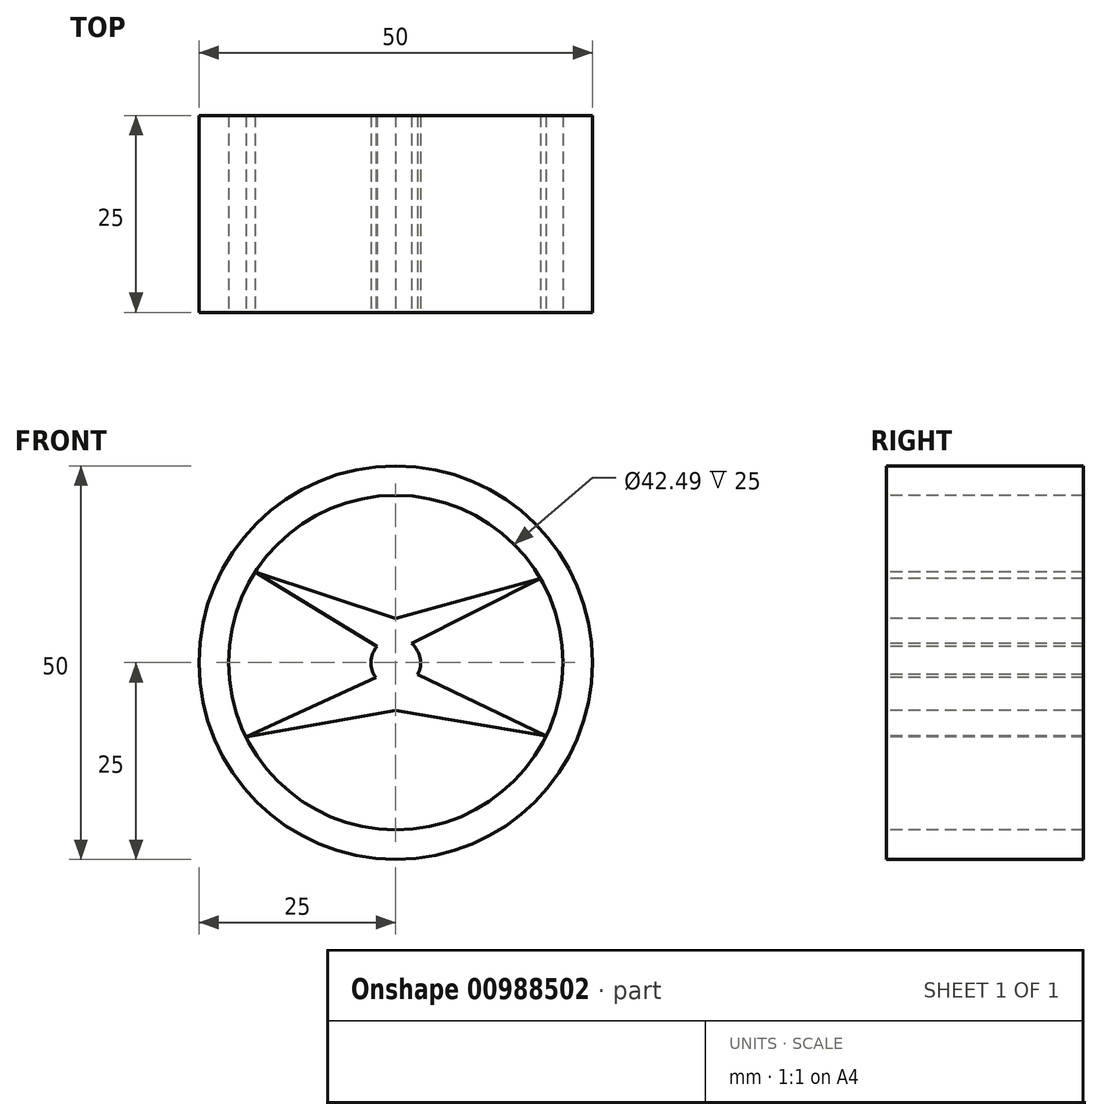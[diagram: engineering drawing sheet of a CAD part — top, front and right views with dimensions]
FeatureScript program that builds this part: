
annotation { "Feature Type Name" : "Feature", "Feature Type Description" : "" }
export const myFeature = defineFeature(function(context is Context, id is Id, definition is map)
    precondition{}
    {
        {
            var Q0;
            Q0=qCreatedBy(makeId("Front.planeOp"),FACE);
            var sketch = newSketch(context, id + "F0", { "sketchPlane" : qUnion([Q0])});
            skCircle(sketch, "E0", {"center": v(0, 0) * mm, "radius": 25 * mm});
            skSolve(sketch);
        }
        {
            var Q0;
            Q0=makeQuery(id+"F0.imprint","IMPRINT",FACE,{"disambiguationData":[TD([[makeQuery(id+"F0.imprint","IMPRINT",EDGE,{"derivedFrom":sQuery(id+"F0.wireOp",EDGE,"E0")}),1.0]])]});
            extrude(context, id + "F1", {"entities" : qUnion([Q0]), "depth" : 25 * mm, "offsetDistance" : 25 * mm});
        }
        {
            var Q0;
            Q0=makeQuery(id+"F1.opExtrude","CAP_FACE",FACE,{"disambiguationData":[OSD([sQuery(id+"F0.wireOp",EDGE,"E0")])],"isStart":false});
            var sketch = newSketch(context, id + "F2", { "sketchPlane" : qUnion([Q0])});
            skCircle(sketch, "E1", {"center": v(0, 0) * mm, "radius": 21.24 * mm});
            skCircle(sketch, "E2", {"center": v(0, 0) * mm, "radius": 3.16 * mm});
            skLineSegment(sketch, "E3", {"start": v(-2.52, -1.9) * mm, "end": v(-19.03, -9.44) * mm});
            skLineSegment(sketch, "E4", {"start": v(-19.03, -9.44) * mm, "end": v(0, -6.08) * mm});
            skLineSegment(sketch, "E5", {"start": v(0, -6.08) * mm, "end": v(19.08, -9.34) * mm});
            skLineSegment(sketch, "E6", {"start": v(19.08, -9.34) * mm, "end": v(2.77, -1.5) * mm});
            skLineSegment(sketch, "E7", {"start": v(2.04, 2.4) * mm, "end": v(18.36, 10.69) * mm});
            skLineSegment(sketch, "E8", {"start": v(18.36, 10.69) * mm, "end": v(0, 5.62) * mm});
            skLineSegment(sketch, "E9", {"start": v(0, 5.62) * mm, "end": v(-17.86, 11.5) * mm});
            skLineSegment(sketch, "E10", {"start": v(-17.86, 11.5) * mm, "end": v(-2.4, 2.06) * mm});
            skSolve(sketch);
        }
        {
            var Q0;
            {var subQ0=sQuery(id+"F2.wireOp",EDGE,"E8");Q0=makeQuery(id+"F2.imprint","IMPRINT",FACE,{"disambiguationData":[TD([[makeQuery(id+"F2.imprint","IMPRINT",EDGE,{"derivedFrom":subQ0}),-1.0]])]});}
            var Q1;
            {var subQ0=sQuery(id+"F2.wireOp",EDGE,"E4");Q1=makeQuery(id+"F2.imprint","IMPRINT",FACE,{"disambiguationData":[TD([[makeQuery(id+"F2.imprint","IMPRINT",EDGE,{"derivedFrom":subQ0}),-1.0]])]});}
            extrude(context, id + "F3", {"entities" : qUnion([Q0, Q1]), "operationType" : NewBodyOperationType.REMOVE, "oppositeDirection" : true, "depth" : 30 * mm, "offsetDistance" : 25 * mm});
        }
        {
            var Q0;
            {var subQ0=sQuery(id+"F2.wireOp",EDGE,"E3");Q0=makeQuery(id+"F2.imprint","IMPRINT",FACE,{"disambiguationData":[TD([[makeQuery(id+"F2.imprint","IMPRINT",EDGE,{"derivedFrom":subQ0}),-1.0]])]});}
            var Q1;
            {var subQ0=sQuery(id+"F2.wireOp",EDGE,"E6");Q1=makeQuery(id+"F2.imprint","IMPRINT",FACE,{"disambiguationData":[TD([[makeQuery(id+"F2.imprint","IMPRINT",EDGE,{"derivedFrom":subQ0}),-1.0]])]});}
            extrude(context, id + "F4", {"entities" : qUnion([Q0, Q1]), "operationType" : NewBodyOperationType.REMOVE, "oppositeDirection" : true, "depth" : 25 * mm, "offsetDistance" : 25 * mm});
        }
    });
